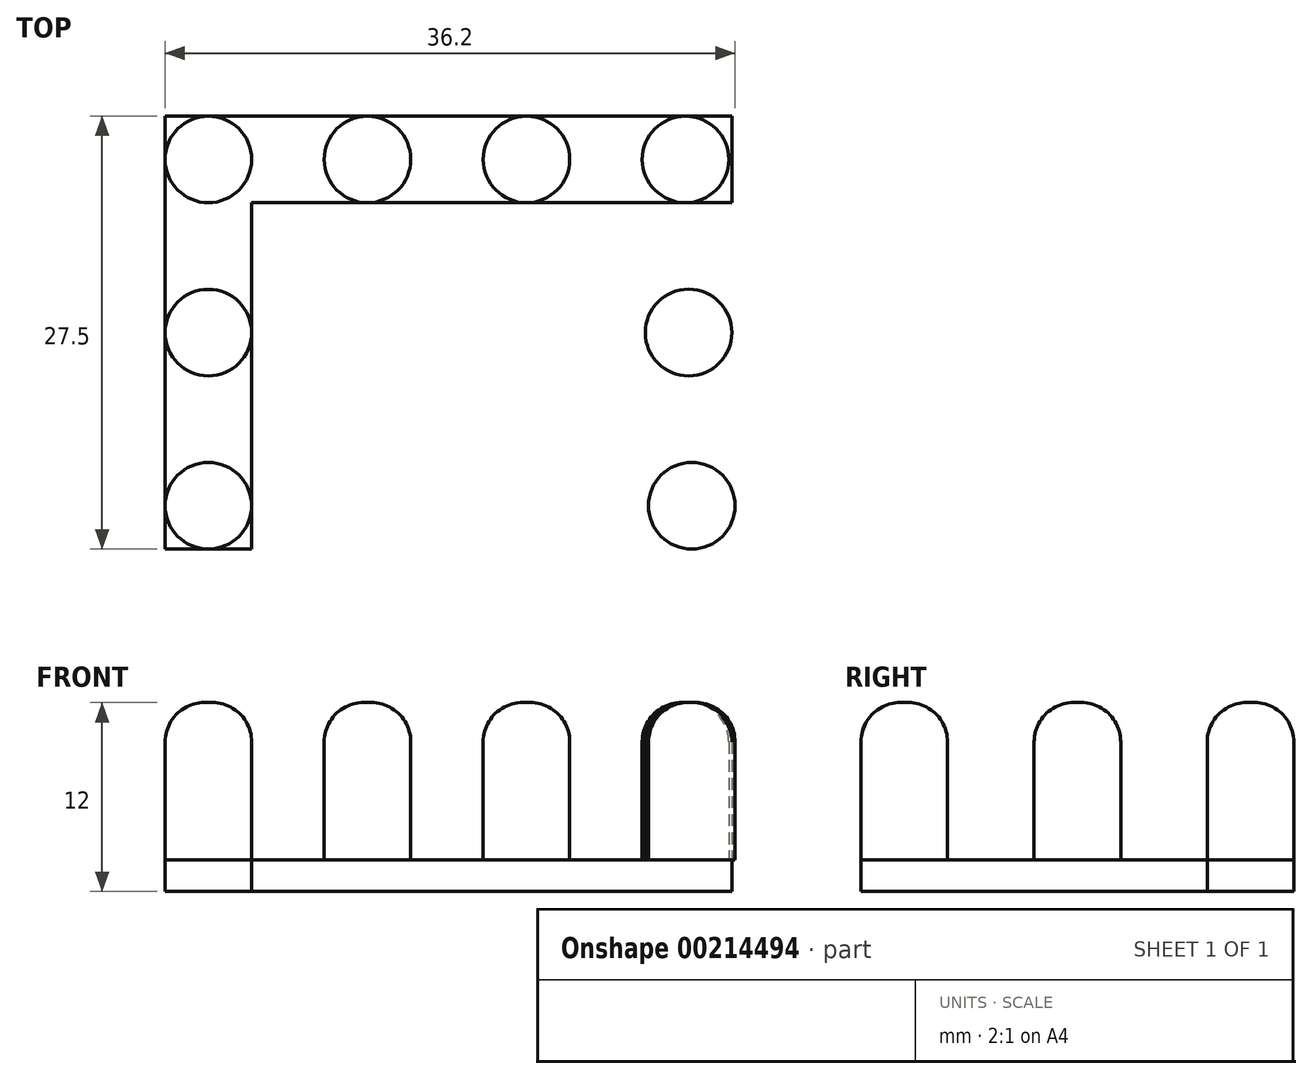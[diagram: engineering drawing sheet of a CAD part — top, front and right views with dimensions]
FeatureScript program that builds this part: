
annotation { "Feature Type Name" : "Feature", "Feature Type Description" : "" }
export const myFeature = defineFeature(function(context is Context, id is Id, definition is map)
    precondition{}
    {
        {
            var Q0;
            Q0=qCreatedBy(makeId("Top.planeOp"),FACE);
            var sketch = newSketch(context, id + "F0", { "sketchPlane" : qUnion([Q0])});
            skLineSegment(sketch, "E0.bottom", {"start": v(-46.79, -16.21) * mm, "end": v(-41.29, -16.21) * mm});
            skLineSegment(sketch, "E0.top", {"start": v(-46.79, -38.21) * mm, "end": v(-41.29, -38.21) * mm});
            skLineSegment(sketch, "E0.left", {"start": v(-46.79, -16.21) * mm, "end": v(-46.79, -38.21) * mm});
            skLineSegment(sketch, "E0.right", {"start": v(-41.29, -16.21) * mm, "end": v(-41.29, -38.21) * mm});
            skLineSegment(sketch, "E1.bottom", {"start": v(-46.79, -16.21) * mm, "end": v(-10.79, -16.21) * mm});
            skLineSegment(sketch, "E1.top", {"start": v(-46.79, -10.71) * mm, "end": v(-10.79, -10.71) * mm});
            skLineSegment(sketch, "E1.left", {"start": v(-46.79, -16.21) * mm, "end": v(-46.79, -10.71) * mm});
            skLineSegment(sketch, "E1.right", {"start": v(-10.79, -16.21) * mm, "end": v(-10.79, -10.71) * mm});
            skLineSegment(sketch, "E2.bottom", {"start": v(-10.79, -16.21) * mm, "end": v(-16.29, -16.21) * mm});
            skLineSegment(sketch, "E2.top", {"start": v(-10.79, -38.21) * mm, "end": v(-16.29, -38.21) * mm});
            skLineSegment(sketch, "E2.left", {"start": v(-10.79, -16.21) * mm, "end": v(-10.79, -38.21) * mm});
            skLineSegment(sketch, "E2.right", {"start": v(-16.29, -16.21) * mm, "end": v(-16.29, -38.21) * mm});
            skSolve(sketch);
        }
        {
            var Q0;
            Q0=makeQuery(id+"F0.imprint","IMPRINT",FACE,{"disambiguationData":[TD([[makeQuery(id+"F0.imprint","IMPRINT",EDGE,{"derivedFrom":sQuery(id+"F0.wireOp",EDGE,"E0.top")}),1.0]])]});
            var Q1;
            Q1=makeQuery(id+"F0.imprint","IMPRINT",FACE,{"disambiguationData":[TD([[makeQuery(id+"F0.imprint","IMPRINT",EDGE,{"derivedFrom":sQuery(id+"F0.wireOp",EDGE,"E1.top")}),-1.0]])]});
            var Q2;
            Q2=makeQuery(id+"F0.imprint","IMPRINT",FACE,{"disambiguationData":[TD([[makeQuery(id+"F0.imprint","IMPRINT",EDGE,{"derivedFrom":sQuery(id+"F0.wireOp",EDGE,"E2.bottom")}),1.0]])]});
            extrude(context, id + "F1", {"entities" : qUnion([Q0, Q1, Q2]), "depth" : 2 * mm});
        }
        {
            var Q0;
            Q0=makeQuery(id+"F1.opExtrude","CAP_FACE",FACE,{"disambiguationData":[OSD([sQuery(id+"F0.wireOp",EDGE,"E0.top"),sQuery(id+"F0.wireOp",EDGE,"E0.left"),sQuery(id+"F0.wireOp",EDGE,"E0.right"),sQuery(id+"F0.wireOp",EDGE,"E1.bottom"),sQuery(id+"F0.wireOp",EDGE,"E1.top"),sQuery(id+"F0.wireOp",EDGE,"E1.left"),sQuery(id+"F0.wireOp",EDGE,"E1.right"),sQuery(id+"F0.wireOp",EDGE,"E2.top"),sQuery(id+"F0.wireOp",EDGE,"E2.left"),sQuery(id+"F0.wireOp",EDGE,"E2.right")])],"isStart":false});
            var sketch = newSketch(context, id + "F2", { "sketchPlane" : qUnion([Q0])});
            skCircle(sketch, "E3", {"center": v(-44.04, -35.46) * mm, "radius": 2.75 * mm});
            skCircle(sketch, "E4.1.0.0", {"center": v(-44.04, -24.46) * mm, "radius": 2.75 * mm});
            skCircle(sketch, "E4.2.0.0", {"center": v(-44.04, -13.46) * mm, "radius": 2.75 * mm});
            skLineSegment(sketch, "E4.direction1", {"start": v(-44.04, -35.46) * mm, "end": v(-44.04, -24.46) * mm, "construction": true});
            skCircle(sketch, "E5.1.0.0", {"center": v(-33.94, -13.46) * mm, "radius": 2.75 * mm});
            skCircle(sketch, "E5.2.0.0", {"center": v(-23.84, -13.46) * mm, "radius": 2.75 * mm});
            skLineSegment(sketch, "E5.direction1", {"start": v(-44.04, -13.46) * mm, "end": v(-33.94, -13.46) * mm, "construction": true});
            skCircle(sketch, "E6.0.3.0", {"center": v(-13.74, -13.46) * mm, "radius": 2.75 * mm});
            skCircle(sketch, "E7.1.0.0", {"center": v(-13.54, -24.46) * mm, "radius": 2.75 * mm});
            skCircle(sketch, "E7.2.0.0", {"center": v(-13.34, -35.46) * mm, "radius": 2.75 * mm});
            skLineSegment(sketch, "E7.direction1", {"start": v(-13.74, -13.46) * mm, "end": v(-13.54, -24.46) * mm, "construction": true});
            skSolve(sketch);
        }
        {
            var Q0;
            Q0 = qSketchRegion(id + "F2", true);
            extrude(context, id + "F3", {"entities" : qUnion([Q0]), "operationType" : NewBodyOperationType.ADD, "depth" : 10 * mm});
        }
        {
            var Q0;
            Q0=makeQuery(id+"F3.opExtrude","CAP_FACE",FACE,{"disambiguationData":[OSD([sQuery(id+"F2.wireOp",EDGE,"E3")])],"isStart":false});
            fillet(context, id + "F4", {"entities" : qUnion([Q0]), "radius" : 2.5 * mm, "tangentPropagation" : true, "allowEdgeOverflow" : false});
        }
        {
            var Q0;
            Q0=makeQuery(id+"F3.opExtrude","CAP_FACE",FACE,{"disambiguationData":[OSD([sQuery(id+"F2.wireOp",EDGE,"E4.1.0.0")])],"isStart":false});
            var Q1;
            Q1=makeQuery(id+"F3.opExtrude","CAP_FACE",FACE,{"disambiguationData":[OSD([sQuery(id+"F2.wireOp",EDGE,"E4.2.0.0")])],"isStart":false});
            var Q2;
            Q2=makeQuery(id+"F3.opExtrude","CAP_FACE",FACE,{"disambiguationData":[OSD([sQuery(id+"F2.wireOp",EDGE,"E5.1.0.0")])],"isStart":false});
            var Q3;
            Q3=makeQuery(id+"F3.opExtrude","CAP_FACE",FACE,{"disambiguationData":[OSD([sQuery(id+"F2.wireOp",EDGE,"E5.2.0.0")])],"isStart":false});
            var Q4;
            Q4=makeQuery(id+"F3.opExtrude","CAP_FACE",FACE,{"disambiguationData":[OSD([sQuery(id+"F2.wireOp",EDGE,"E6.0.3.0")])],"isStart":false});
            var Q5;
            Q5=makeQuery(id+"F3.opExtrude","CAP_FACE",FACE,{"disambiguationData":[OSD([sQuery(id+"F2.wireOp",EDGE,"E7.1.0.0")])],"isStart":false});
            var Q6;
            Q6=makeQuery(id+"F3.opExtrude","CAP_FACE",FACE,{"disambiguationData":[OSD([sQuery(id+"F2.wireOp",EDGE,"E7.2.0.0")])],"isStart":false});
            fillet(context, id + "F5", {"entities" : qUnion([Q0, Q1, Q2, Q3, Q4, Q5, Q6]), "radius" : 2.5 * mm, "tangentPropagation" : true, "allowEdgeOverflow" : false});
        }
    });
